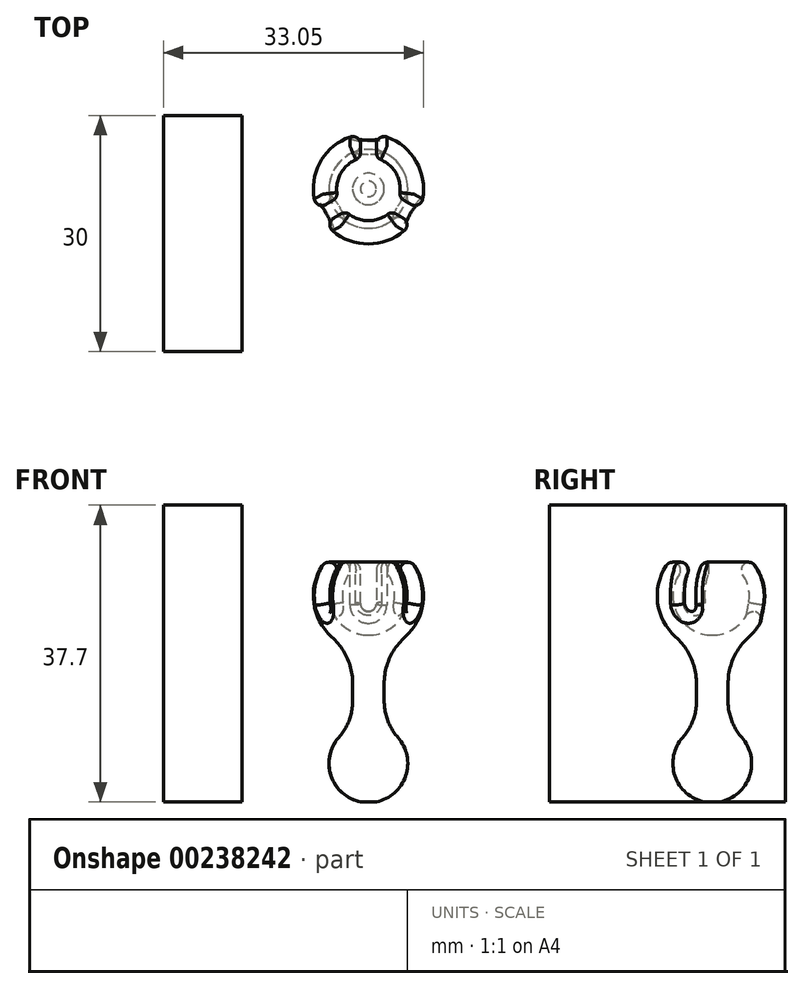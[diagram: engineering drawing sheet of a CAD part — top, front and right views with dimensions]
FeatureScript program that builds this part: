
annotation { "Feature Type Name" : "Feature", "Feature Type Description" : "" }
export const myFeature = defineFeature(function(context is Context, id is Id, definition is map)
    precondition{}
    {
        {
            var Q0;
            Q0=qCreatedBy(makeId("Front.planeOp"),FACE);
            var sketch = newSketch(context, id + "F0", { "sketchPlane" : qUnion([Q0])});
            skArc(sketch, "E0", {"start": v(-4.2, 2.72) * mm, "mid": v(-4.4, -2.39) * mm, "end": v(0, -5) * mm});
            skArc(sketch, "E1", {"start": v(-5.87, 3.81) * mm, "mid": v(-6.57, -2.42) * mm, "end": v(-2, -6.7) * mm});
            skLineSegment(sketch, "E2", {"start": v(-4.2, 2.72) * mm, "end": v(-5.87, 3.81) * mm, "construction": true});
            skLineSegment(sketch, "E3", {"start": v(0, -5) * mm, "end": v(0, -13.57) * mm, "construction": true});
            skArc(sketch, "E4", {"start": v(-4.2, 2.72) * mm, "mid": v(-4.49, 4.1) * mm, "end": v(-5.87, 3.81) * mm});
            skPoint(sketch, "E5.endSnap0", {"position": v(0, -6.78) * mm});
            skLineSegment(sketch, "E6.trimOffspring", {"start": v(0, -5) * mm, "end": v(0, -7) * mm});
            skLineSegment(sketch, "E7", {"start": v(-2, -6.7) * mm, "end": v(-2, -16.7) * mm});
            skLineSegment(sketch, "E8", {"start": v(0, -15) * mm, "end": v(0, -7) * mm});
            skArc(sketch, "E9", {"start": v(-2, -16.7) * mm, "mid": v(-4.97, -21.82) * mm, "end": v(-1, -26.19) * mm});
            skLineSegment(sketch, "E10", {"start": v(0, -15) * mm, "end": v(0, -26.3) * mm});
            skLineSegment(sketch, "E11", {"start": v(-1, -26.19) * mm, "end": v(0, -26.19) * mm});
            skCircle(sketch, "E12", {"center": v(0, 6.54) * mm, "radius": 5 * mm, "construction": true});
            skLineSegment(sketch, "E13", {"start": v(-5, 11.6) * mm, "end": v(-5, -24.85) * mm, "construction": true});
            skCircle(sketch, "E14", {"center": v(0, 0) * mm, "radius": 5 * mm, "construction": true});
            skLineSegment(sketch, "E15", {"start": v(-4.2, 2.72) * mm, "end": v(-4.2, -8.13) * mm, "construction": true});
            skSolve(sketch);
        }
        {
            var Q0;
            Q0=makeQuery(id+"F0.imprint","IMPRINT",FACE,{"disambiguationData":[TD([[makeQuery(id+"F0.imprint","IMPRINT",EDGE,{"derivedFrom":sQuery(id+"F0.wireOp",EDGE,"E0")}),-1.0]])]});
            var Q1;
            Q1=sQuery(id+"F0.wireOp",EDGE,"E8");
            revolve(context, id + "F1", {"entities" : qUnion([Q0]), "axis" : qUnion([Q1]), "revolveType" : RevolveType.FULL});
        }
        {
            var Q0;
            Q0=qCreatedBy(makeId("Top.planeOp"),FACE);
            cPlane(context, id + "F2", {"entities" : qUnion([Q0]), "cplaneType" : CPlaneType.OFFSET, "offset" : 5 * mm, "width" : 150 * mm, "height" : 150 * mm});
        }
        {
            var Q0;
            Q0=qCreatedBy(id+"F2.planeOp",FACE);
            var sketch = newSketch(context, id + "F3", { "sketchPlane" : qUnion([Q0])});
            skLineSegment(sketch, "E16", {"start": v(0, 0) * mm, "end": v(0, 9.47) * mm, "construction": true});
            skLineSegment(sketch, "E17.bottom", {"start": v(1, 9.47) * mm, "end": v(-1, 9.47) * mm});
            skLineSegment(sketch, "E17.top", {"start": v(1, 0) * mm, "end": v(-1, 0) * mm});
            skLineSegment(sketch, "E17.left", {"start": v(1, 9.47) * mm, "end": v(1, 0) * mm});
            skLineSegment(sketch, "E17.right", {"start": v(-1, 9.47) * mm, "end": v(-1, 0) * mm});
            skPoint(sketch, "E17.middle", {"position": v(0, 4.73) * mm});
            skPoint(sketch, "E18.1.0", {"position": v(-4.1, -2.37) * mm});
            skLineSegment(sketch, "E18.1.1", {"start": v(-7.7, -5.6) * mm, "end": v(0.5, -0.87) * mm});
            skLineSegment(sketch, "E18.1.2", {"start": v(-8.7, -3.87) * mm, "end": v(-0.5, 0.87) * mm});
            skLineSegment(sketch, "E18.1.3", {"start": v(-0.5, 0.87) * mm, "end": v(0.5, -0.87) * mm});
            skLineSegment(sketch, "E18.1.4", {"start": v(0, 0) * mm, "end": v(-8.2, -4.73) * mm, "construction": true});
            skLineSegment(sketch, "E18.1.5", {"start": v(-8.7, -3.87) * mm, "end": v(-7.7, -5.6) * mm});
            skPoint(sketch, "E18.2.0", {"position": v(4.1, -2.37) * mm});
            skLineSegment(sketch, "E18.2.1", {"start": v(8.7, -3.87) * mm, "end": v(0.5, 0.87) * mm});
            skLineSegment(sketch, "E18.2.2", {"start": v(7.7, -5.6) * mm, "end": v(-0.5, -0.87) * mm});
            skLineSegment(sketch, "E18.2.3", {"start": v(-0.5, -0.87) * mm, "end": v(0.5, 0.87) * mm});
            skLineSegment(sketch, "E18.2.4", {"start": v(0, 0) * mm, "end": v(8.2, -4.73) * mm, "construction": true});
            skLineSegment(sketch, "E18.2.5", {"start": v(7.7, -5.6) * mm, "end": v(8.7, -3.87) * mm});
            skPoint(sketch, "E18.center", {"position": v(0, 0) * mm});
            skSolve(sketch);
        }
        {
            var Q0;
            Q0=qSketchRegion(id+"F3",true);
            extrude(context, id + "F4", {"entities" : qUnion([Q0]), "operationType" : NewBodyOperationType.REMOVE, "oppositeDirection" : true, "depth" : 7 * mm});
        }
        {
            var Q0;
            Q0=makeQuery(id+"F4.boolean.opBoolean","COPY",EDGE,{"derivedFrom":makeQuery(id+"F4.opExtrude","CAP_EDGE",EDGE,{"disambiguationData":[OSD([sQuery(id+"F3.wireOp",EDGE,"E18.1.2")])],"isStart":false})});
            var Q1;
            Q1=makeQuery(id+"F4.boolean.opBoolean","COPY",EDGE,{"derivedFrom":makeQuery(id+"F4.opExtrude","CAP_EDGE",EDGE,{"disambiguationData":[OSD([sQuery(id+"F3.wireOp",EDGE,"E18.1.1")])],"isStart":false})});
            var Q2;
            Q2=makeQuery(id+"F4.boolean.opBoolean","COPY",EDGE,{"derivedFrom":makeQuery(id+"F4.opExtrude","CAP_EDGE",EDGE,{"disambiguationData":[OSD([sQuery(id+"F3.wireOp",EDGE,"E18.2.1")])],"isStart":false})});
            var Q3;
            Q3=makeQuery(id+"F4.boolean.opBoolean","COPY",EDGE,{"derivedFrom":makeQuery(id+"F4.opExtrude","CAP_EDGE",EDGE,{"disambiguationData":[OSD([sQuery(id+"F3.wireOp",EDGE,"E18.2.2")])],"isStart":false})});
            var Q4;
            Q4=makeQuery(id+"F4.boolean.opBoolean","COPY",EDGE,{"derivedFrom":makeQuery(id+"F4.opExtrude","CAP_EDGE",EDGE,{"disambiguationData":[OSD([sQuery(id+"F3.wireOp",EDGE,"E17.right")])],"isStart":false})});
            var Q5;
            Q5=makeQuery(id+"F4.boolean.opBoolean","COPY",EDGE,{"derivedFrom":makeQuery(id+"F4.opExtrude","CAP_EDGE",EDGE,{"disambiguationData":[OSD([sQuery(id+"F3.wireOp",EDGE,"E17.left")])],"isStart":false})});
            fillet(context, id + "F5", {"entities" : qUnion([Q0, Q1, Q2, Q3, Q4, Q5]), "radius" : 1 * mm, "tangentPropagation" : true, "allowEdgeOverflow" : false});
        }
        {
            var Q0;
            Q0=makeQuery(id+"F4.boolean.opBoolean","INTERSECT",EDGE,{"derivedFrom":[makeQuery(id+"F1.opRevolve","SWEPT_FACE",FACE,{"disambiguationData":[OSD([sQuery(id+"F0.wireOp",EDGE,"E1")])]}),makeQuery(id+"F4.opExtrude","SWEPT_FACE",FACE,{"disambiguationData":[OSD([sQuery(id+"F3.wireOp",EDGE,"E18.2.1")])]})]});
            var Q1;
            Q1=makeQuery(id+"F4.boolean.opBoolean","INTERSECT",EDGE,{"derivedFrom":[makeQuery(id+"F1.opRevolve","SWEPT_FACE",FACE,{"disambiguationData":[OSD([sQuery(id+"F0.wireOp",EDGE,"E1")])]}),makeQuery(id+"F4.opExtrude","SWEPT_FACE",FACE,{"disambiguationData":[OSD([sQuery(id+"F3.wireOp",EDGE,"E17.right")])]})]});
            var Q2;
            Q2=makeQuery(id+"F4.boolean.opBoolean","INTERSECT",EDGE,{"derivedFrom":[makeQuery(id+"F1.opRevolve","SWEPT_FACE",FACE,{"disambiguationData":[OSD([sQuery(id+"F0.wireOp",EDGE,"E1")])]}),makeQuery(id+"F4.opExtrude","SWEPT_FACE",FACE,{"disambiguationData":[OSD([sQuery(id+"F3.wireOp",EDGE,"E18.1.2")])]})]});
            fillet(context, id + "F6", {"entities" : qUnion([Q0, Q1, Q2]), "radius" : 1 * mm, "tangentPropagation" : true, "allowEdgeOverflow" : false});
        }
        {
            var Q0;
            Q0=makeQuery(id+"F1.opRevolve","SWEPT_EDGE",EDGE,{"disambiguationData":[OSD([sQuery(id+"F0.wireOp",EDGE,"E1"),sQuery(id+"F0.wireOp",EDGE,"E7")])]});
            fillet(context, id + "F7", {"entities" : qUnion([Q0]), "radius" : 8 * mm, "tangentPropagation" : true, "allowEdgeOverflow" : false});
        }
        {
            var Q0;
            Q0=makeQuery(id+"F1.opRevolve","SWEPT_EDGE",EDGE,{"disambiguationData":[OSD([sQuery(id+"F0.wireOp",EDGE,"E7"),sQuery(id+"F0.wireOp",EDGE,"ywg5SL3T-TYOw-sGt6-3Rzi-PARAZnVLxAsf")])]});
            fillet(context, id + "F8", {"entities" : qUnion([Q0]), "radius" : 7 * mm, "tangentPropagation" : true, "allowEdgeOverflow" : false});
        }
        {
            var Q0;
            Q0=makeQuery(id+"F1.opRevolve","SWEPT_FACE",FACE,{"disambiguationData":[OSD([sQuery(id+"F0.wireOp",EDGE,"E11")])]});
            var sketch = newSketch(context, id + "F9", { "sketchPlane" : qUnion([Q0])});
            skLineSegment(sketch, "E19.bottom", {"start": v(-26.05, -9.32) * mm, "end": v(-16.05, -9.32) * mm});
            skLineSegment(sketch, "E19.top", {"start": v(-26.05, 20.68) * mm, "end": v(-16.05, 20.68) * mm});
            skLineSegment(sketch, "E19.left", {"start": v(-26.05, -9.32) * mm, "end": v(-26.05, 20.68) * mm});
            skLineSegment(sketch, "E19.right", {"start": v(-16.05, -9.32) * mm, "end": v(-16.05, 20.68) * mm});
            skSolve(sketch);
        }
        {
            var Q0;
            Q0=makeQuery(id+"F9.imprint","IMPRINT",FACE,{"disambiguationData":[TD([[makeQuery(id+"F9.imprint","IMPRINT",EDGE,{"derivedFrom":sQuery(id+"F9.wireOp",EDGE,"E19.bottom")}),1.0]])]});
            extrude(context, id + "F10", {"entities" : qUnion([Q0]), "oppositeDirection" : true, "depth" : 37.7 * mm});
        }
    });
